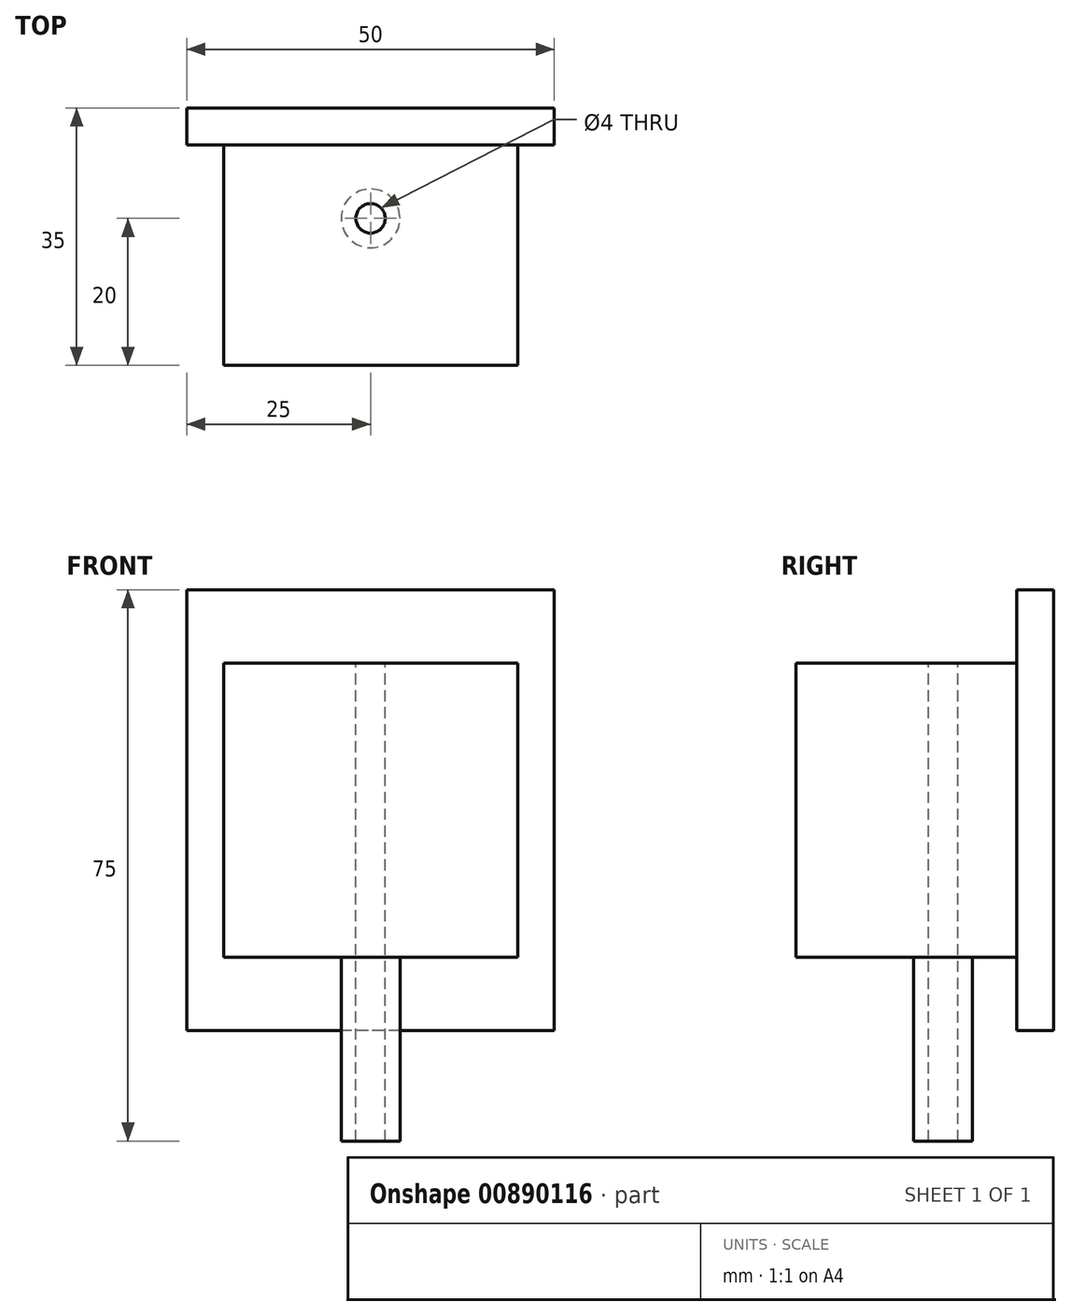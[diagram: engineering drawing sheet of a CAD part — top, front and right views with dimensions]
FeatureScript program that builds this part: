
annotation { "Feature Type Name" : "Feature", "Feature Type Description" : "" }
export const myFeature = defineFeature(function(context is Context, id is Id, definition is map)
    precondition{}
    {
        {
            var Q0;
            Q0=qCreatedBy(makeId("Front.planeOp"),FACE);
            var sketch = newSketch(context, id + "F0", { "sketchPlane" : qUnion([Q0])});
            skLineSegment(sketch, "E0.bottom", {"start": v(20, 20) * mm, "end": v(-20, 20) * mm});
            skLineSegment(sketch, "E0.top", {"start": v(20, -20) * mm, "end": v(-20, -20) * mm});
            skLineSegment(sketch, "E0.left", {"start": v(20, 20) * mm, "end": v(20, -20) * mm});
            skLineSegment(sketch, "E0.right", {"start": v(-20, 20) * mm, "end": v(-20, -20) * mm});
            skPoint(sketch, "E0.middle", {"position": v(0, 0) * mm});
            skSolve(sketch);
        }
        {
            var Q0;
            Q0 = qSketchRegion(id + "F0", true);
            extrude(context, id + "F1", {"entities" : qUnion([Q0]), "depth" : 30 * mm, "offsetDistance" : 25 * mm});
        }
        {
            var Q0;
            Q0=makeQuery(id+"F1.opExtrude","SWEPT_FACE",FACE,{"disambiguationData":[OSD([sQuery(id+"F0.wireOp",EDGE,"E0.top")])]});
            var sketch = newSketch(context, id + "F2", { "sketchPlane" : qUnion([Q0])});
            skCircle(sketch, "E1", {"center": v(0, 10) * mm, "radius": 4 * mm});
            skCircle(sketch, "E2", {"center": v(0, 10) * mm, "radius": 2 * mm});
            skSolve(sketch);
        }
        {
            var Q0;
            Q0 = qSketchRegion(id + "F2", true);
            extrude(context, id + "F3", {"entities" : qUnion([Q0]), "operationType" : NewBodyOperationType.ADD, "depth" : 25 * mm, "offsetDistance" : 25 * mm});
        }
        {
            var Q0;
            Q0=makeQuery(id+"F3.boolean.opBoolean","SPLIT",FACE,{"disambiguationData":[TD([makeQuery(id+"F3.opExtrude","SWEPT_FACE",FACE,{"disambiguationData":[OSD([sQuery(id+"F2.wireOp",EDGE,"E2")])]})])],"derivedFrom":makeQuery(id+"F1.opExtrude","SWEPT_FACE",FACE,{"disambiguationData":[OSD([sQuery(id+"F0.wireOp",EDGE,"E0.top")])]})});
            extrude(context, id + "F4", {"entities" : qUnion([Q0]), "operationType" : NewBodyOperationType.REMOVE, "oppositeDirection" : true, "depth" : 40 * mm, "offsetDistance" : 25 * mm});
        }
        {
            var Q0;
            Q0=qCreatedBy(makeId("Right.planeOp"),FACE);
            var sketch = newSketch(context, id + "F5", { "sketchPlane" : qUnion([Q0])});
            skLineSegment(sketch, "E3", {"start": v(0, 0) * mm, "end": v(0, 30) * mm});
            skLineSegment(sketch, "E4", {"start": v(5, 30) * mm, "end": v(0, 30) * mm});
            skLineSegment(sketch, "E5", {"start": v(5, 30) * mm, "end": v(5, -30) * mm});
            skLineSegment(sketch, "E6", {"start": v(0, -30) * mm, "end": v(5, -30) * mm});
            skLineSegment(sketch, "E7", {"start": v(0, -30) * mm, "end": v(0, 0) * mm});
            skSolve(sketch);
        }
        {
            var Q0;
            Q0 = qSketchRegion(id + "F5", true);
            extrude(context, id + "F6", {"entities" : qUnion([Q0]), "operationType" : NewBodyOperationType.ADD, "depth" : 50 * mm, "offsetDistance" : 25 * mm, "symmetric" : true});
        }
    });
